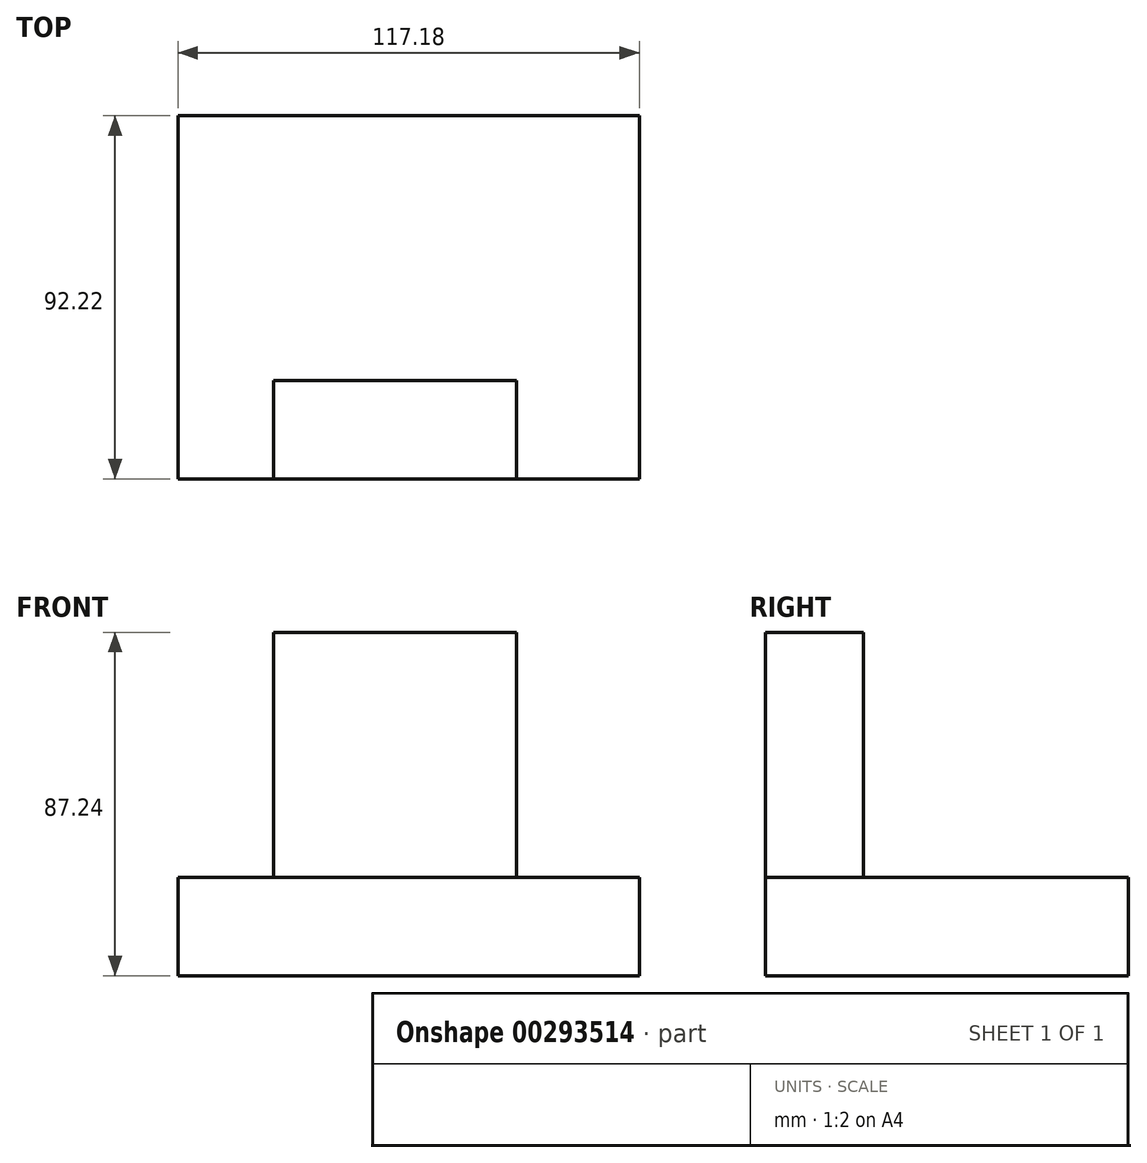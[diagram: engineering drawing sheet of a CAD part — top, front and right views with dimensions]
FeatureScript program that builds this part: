
annotation { "Feature Type Name" : "Feature", "Feature Type Description" : "" }
export const myFeature = defineFeature(function(context is Context, id is Id, definition is map)
    precondition{}
    {
        {
            var Q0;
            Q0=qCreatedBy(makeId("Top.planeOp"),FACE);
            var sketch = newSketch(context, id + "F0", { "sketchPlane" : qUnion([Q0])});
            skLineSegment(sketch, "E0.bottom", {"start": v(58.6, -46.1) * mm, "end": v(-58.6, -46.1) * mm});
            skLineSegment(sketch, "E0.top", {"start": v(58.6, 46.1) * mm, "end": v(-58.6, 46.1) * mm});
            skLineSegment(sketch, "E0.left", {"start": v(58.6, -46.1) * mm, "end": v(58.6, 46.1) * mm});
            skLineSegment(sketch, "E0.right", {"start": v(-58.6, -46.1) * mm, "end": v(-58.6, 46.1) * mm});
            skPoint(sketch, "E0.middle", {"position": v(0, 0) * mm});
            skSolve(sketch);
        }
        {
            var Q0;
            Q0 = qSketchRegion(id + "F0", true);
            extrude(context, id + "F1", {"entities" : qUnion([Q0]), "depth" : 25 * mm});
        }
        {
            var Q0;
            Q0=makeQuery(id+"F1.opExtrude","SWEPT_FACE",FACE,{"disambiguationData":[OSD([sQuery(id+"F0.wireOp",EDGE,"E0.bottom")])]});
            var sketch = newSketch(context, id + "F2", { "sketchPlane" : qUnion([Q0])});
            skLineSegment(sketch, "E1.bottom", {"start": v(-34.26, 25) * mm, "end": v(27.4, 25) * mm});
            skLineSegment(sketch, "E1.top", {"start": v(-34.26, 87.24) * mm, "end": v(27.4, 87.24) * mm});
            skLineSegment(sketch, "E1.left", {"start": v(-34.26, 25) * mm, "end": v(-34.26, 87.24) * mm});
            skLineSegment(sketch, "E1.right", {"start": v(27.4, 25) * mm, "end": v(27.4, 87.24) * mm});
            skSolve(sketch);
        }
        {
            var Q0;
            Q0 = qSketchRegion(id + "F2", true);
            extrude(context, id + "F3", {"entities" : qUnion([Q0]), "oppositeDirection" : true, "depth" : 25 * mm});
        }
    });
